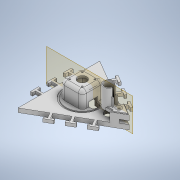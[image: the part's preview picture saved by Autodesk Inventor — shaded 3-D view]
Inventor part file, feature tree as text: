
AUTODESK INVENTOR PART (.ipt)
format: ipt  version: 2022.3 (Build 263350000, 350)  size: 775,168 bytes
history: native  units: mm
features: extrude x29, sketch x25, fillet x7, thicken_offset x6, projected_geometry x5, hole x1, plane x1
ambient origin geometry x8: Origin, YZ Plane, XZ Plane, XY Plane, X Axis, Y Axis, Z Axis, Center Point
bodies: Solid1 (feature_tree)
feature tree (74):
  sketch  "Sketch1"  dims[d1=200.0mm d2=35.0mm]
  extrude  "Extrusion1"  Depth=35.0mm
  extrude  "Extrusion2"  Depth=5.0mm
  sketch  "Sketch2"  dims[d3=5.0mm d4=5.0mm]
  extrude  "Extrusion3"  Depth=40.0mm
  extrude  "Extrusion4"  Depth=40.0mm
  extrude  "Extrusion5"  Depth=10.0mm TaperAngle=0.0deg
  extrude  "Extrusion6"  Depth=42.0mm
  extrude  "Extrusion7"  Depth=6.0mm
  extrude  "Extrusion8"  Depth=10.0mm
  hole  "Hole1"  [1 undecoded]
  fillet  "Fillet1"  Radius=3.0mm
  sketch  "Sketch9"  dims[d43=18.0mm d44=40.0mm d45=0.0mm d46=3.0mm]
  extrude  "Extrusion9"  Depth=10.0mm
  extrude  "Extrusion10"  Depth=80.0mm
  sketch  "Sketch10"  dims[d47=1.5mm d48=0.0mm d49=10.0mm]
  extrude  "Extrusion11"  Depth=2.0mm TaperAngle=0.0deg
  extrude  "Extrusion12"  Depth=22.0mm
  plane  "Work Plane1"
  extrude  "Extrusion13"  Depth=5.0mm
  extrude  "Extrusion14"  Depth=10.0mm
  extrude  "Extrusion15"  TaperAngle=180.0deg  [1 undecoded]
  sketch  "Sketch21"  dims[d59=5.0mm d60=0.0mm d61=31.0mm]
  extrude  "Extrusion18"  Depth=2.0mm
  extrude  "Extrusion19"  Depth=6.0mm
  extrude  "Extrusion20"  Depth=15.0mm TaperAngle=0.0deg
  thicken_offset  "Thicken1"
  fillet  "Fillet7"  Radius=9.0mm
  thicken_offset  "Thicken2"
  thicken_offset  "Thicken3"
  thicken_offset  "Thicken4"
  extrude  "Extrusion21"  Depth=4.0mm
  thicken_offset  "Thicken5"
  extrude  "Extrusion22"  Depth=12.0mm TaperAngle=0.0deg
  fillet  "Fillet8"  Radius=10.0mm
  extrude  "Extrusion23"  Depth=12.0mm
  extrude  "Extrusion24"  Depth=2.0mm
  extrude  "Extrusion25"  Depth=10.0mm TaperAngle=0.0deg
  fillet  "Fillet9"  Radius=45.0mm
  fillet  "Fillet10"  Radius=10.0mm
  extrude  "Extrusion26"  Depth=10.0mm
  extrude  "Extrusion27"  Depth=4.0mm
  extrude  "Extrusion28"  Depth=10.0mm
  extrude  "Extrusion29"  Depth=10.0mm
  fillet  "Fillet11"  Radius=1.388mm
  extrude  "Extrusion31"  Depth=10.0mm
  fillet  "Fillet12"  Radius=8.0mm
  extrude  "Extrusion32"  Depth=8.0mm
  thicken_offset  "Thicken6"
  sketch  "Sketch3"  dims[d5=20.0mm d6=30.0mm d8=40.0mm d9=30.0mm d11=40.0mm]
  sketch  "Sketch4"  dims[d14=30.0mm d16=240.0deg d18=30.0mm d20=40.0mm d21=30.0mm d23=40.0mm]
  sketch  "Sketch5"  dims[d26=30.0mm d28=40.0mm d29=30.0mm d31=40.0mm d34=10.0mm d35=0.0mm]
  sketch  "Sketch6"  dims[d36=2.5mm d37=0.0mm d38=42.0mm]
  projected_geometry  "Projected Loop1"
  sketch  "Sketch7"  dims[d39=42.0mm d40=6.0mm]
  projected_geometry  "Projected Loop2"
  sketch  "Sketch8"  dims[d41=20.0mm d42=10.0mm]
  sketch  "Sketch14"  dims[d50=3.0mm d51=0.0mm d52=80.0mm]
  sketch  "Sketch15"  dims[d53=4.0mm d54=2.0mm d55=0.0mm]
  sketch  "Sketch16"  dims[d56=0.0mm d57=0.0mm d58=22.0mm]
  projected_geometry  "Projected Loop3"
  projected_geometry  "Projected Loop4"
  sketch  "Sketch22"  dims[d62=31.0mm]
  sketch  "Sketch23"  dims[d63=2.4mm d64=6.0mm d65=4.0mm d66=2.0mm d67=90.0deg d68=5.0mm d69=0.0mm d70=10.0mm]
  sketch  "Sketch24"  dims[d72=50.0mm d73=180.0deg]
  sketch  "Sketch25"  dims[d74=22.0mm d75=2.0mm]
  sketch  "Sketch26"  dims[d76=6.0mm d77=6.0mm]
  sketch  "Sketch27"  dims[d78=63.0mm d79=0.0mm d80=15.0mm d81=0.0mm d84=9.0mm d85=0.0mm]
  sketch  "Sketch28"  dims[d86=4.0mm d87=0.0mm d89=0.419mm]
  sketch  "Sketch29"  dims[d95=15.0mm d96=12.0mm d97=12.0mm d98=0.0mm d99=0.0mm d100=10.0mm d101=0.0mm]
  projected_geometry  "Projected Loop7"
  sketch  "Sketch30"  dims[d102=0.0mm d103=0.0mm d119=12.0mm]
  sketch  "Sketch31"  dims[d120=18.0mm d121=2.0mm]
  sketch  "Sketch33"  dims[d122=20.0mm d123=0.0mm d124=45.0mm d125=0.0mm d126=45.0mm d127=0.0mm d128=10.0mm d129=10.0mm d130=4.0mm d131=1.388mm d132=1.388mm d133=1.388mm d134=1.388mm d135=8.0mm d136=8.0mm d137=10.0mm d138=0.0mm d139=9.0mm d140=9.0mm d141=60.0mm d142=18.0mm d143=3.0mm d144=0.0mm d145=2.0mm d146=6.0mm d147=18.0mm d148=0.0mm d149=18.0mm d150=8.0mm d151=0.0mm d152=0.0mm d153=0.0mm d154=0.0mm d155=4.0mm d156=2.0mm d157=4.0mm d160=4.0mm d161=3.0mm d162=4.0mm d165=1.0mm d169=3.0mm d170=4.0mm d171=1.0mm d172=4.0mm d173=20.0mm d174=0.0mm d175=1.5mm d176=2.0mm d177=0.0mm d178=2.0mm d179=18.0mm d180=2.0mm d181=0.0mm d182=16.0mm d183=6.0mm d184=10.0mm d185=0.0mm d188=8.0mm d189=8.2mm d190=20.0mm d191=4.0mm d192=0.0mm d193=2.0mm d194=10.0mm d195=0.0mm d196=0.5mm d197=0.5mm d71=20.594885mm d166=0.872665mm d167=0.5mm d168=0.872665mm]
note: 2 required parameter values undecoded (feature->parameter linkage not recoverable at this tier; creation-order binding heuristic only, values carry confidence <= 0.55)
